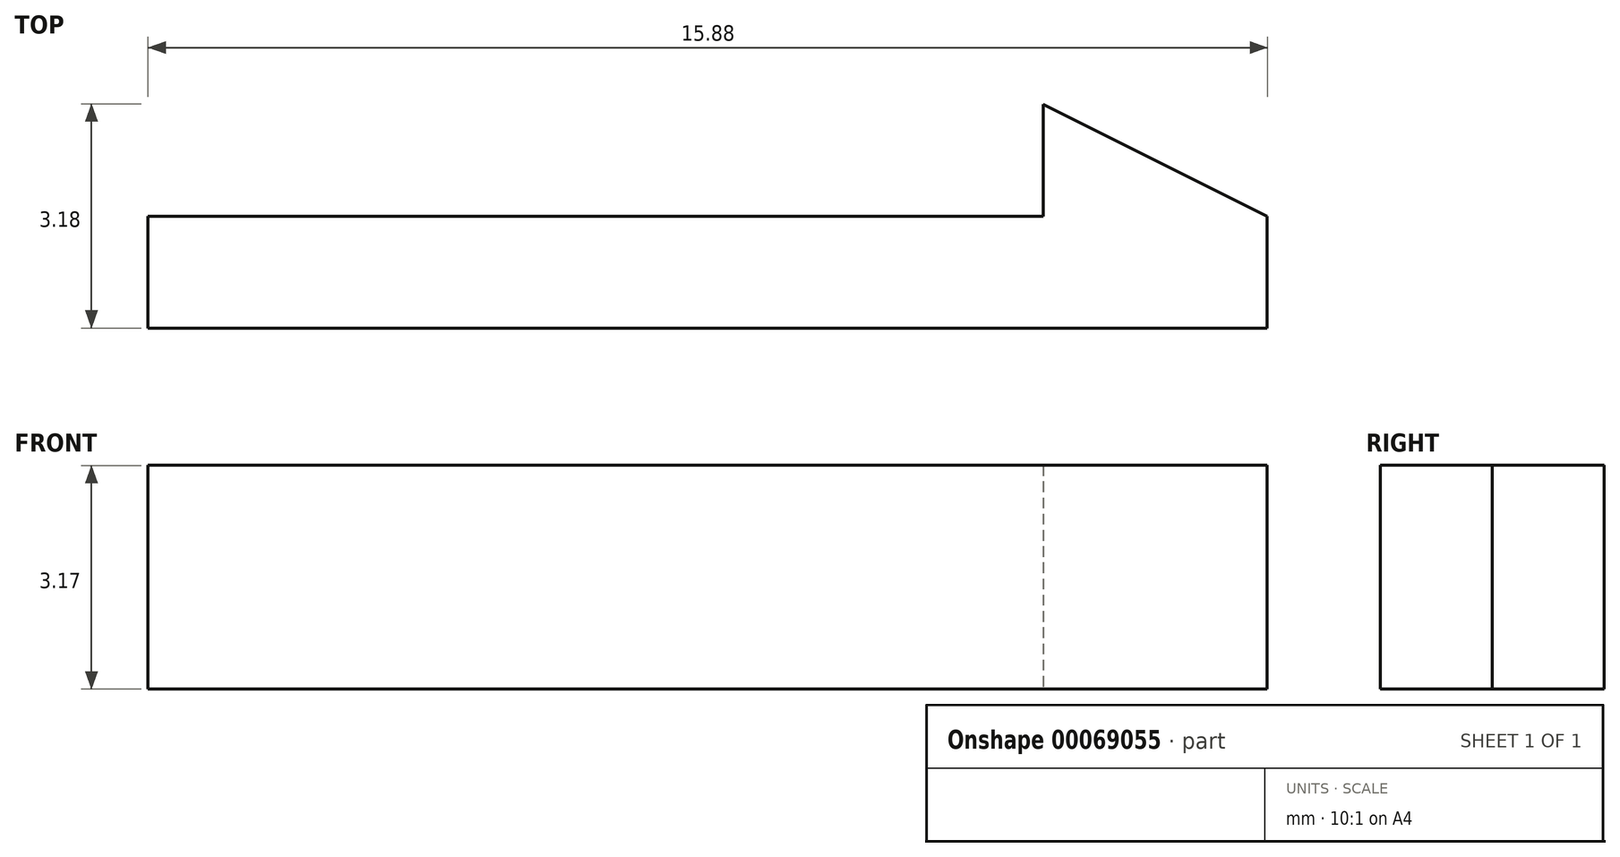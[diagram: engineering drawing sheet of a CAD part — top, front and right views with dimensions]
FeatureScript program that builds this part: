
annotation { "Feature Type Name" : "Feature", "Feature Type Description" : "" }
export const myFeature = defineFeature(function(context is Context, id is Id, definition is map)
    precondition{}
    {
        {
            var Q0;
            Q0=qCreatedBy(makeId("Top.planeOp"),FACE);
            var sketch = newSketch(context, id + "F0", { "sketchPlane" : qUnion([Q0])});
            skLineSegment(sketch, "E0.bottom", {"start": v(0, 0) * mm, "end": v(15.88, 0) * mm});
            skLineSegment(sketch, "E0.top", {"start": v(0, 1.59) * mm, "end": v(15.88, 1.59) * mm});
            skLineSegment(sketch, "E0.left", {"start": v(0, 0) * mm, "end": v(0, 1.59) * mm});
            skLineSegment(sketch, "E0.right", {"start": v(15.88, 0) * mm, "end": v(15.88, 1.59) * mm});
            skLineSegment(sketch, "E1", {"start": v(12.7, 1.59) * mm, "end": v(12.7, 3.17) * mm});
            skLineSegment(sketch, "E2", {"start": v(12.7, 3.17) * mm, "end": v(15.88, 1.59) * mm});
            skSolve(sketch);
        }
        {
            var Q0;
            Q0 = qSketchRegion(id + "F0", true);
            extrude(context, id + "F1", {"entities" : qUnion([Q0]), "depth" : 3.17 * mm});
        }
    });
